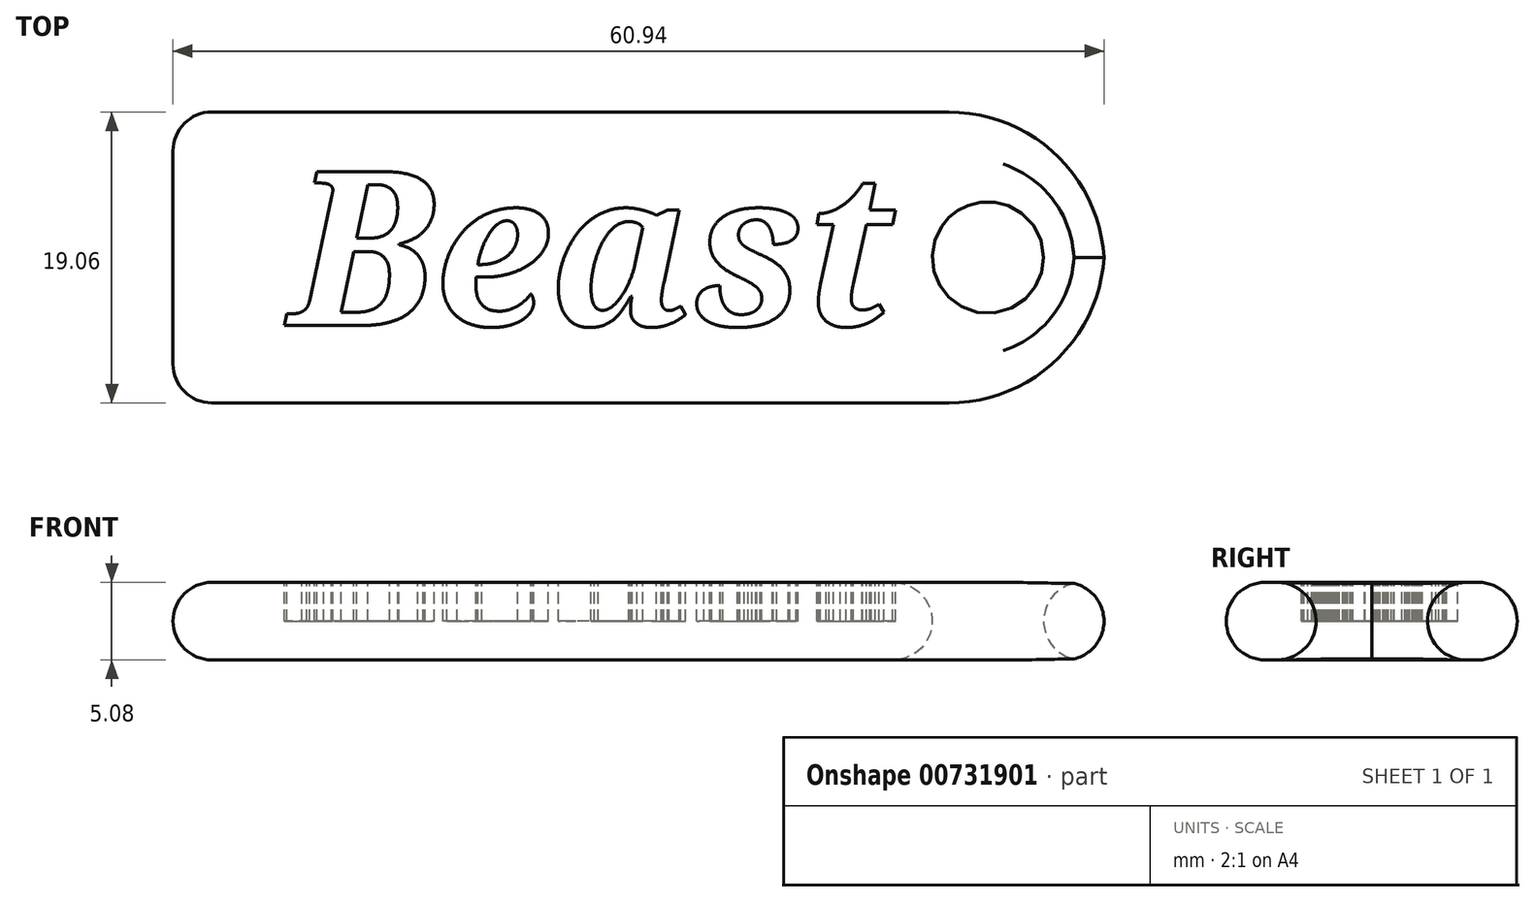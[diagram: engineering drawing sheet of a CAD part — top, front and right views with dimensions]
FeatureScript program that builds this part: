
annotation { "Feature Type Name" : "Feature", "Feature Type Description" : "" }
export const myFeature = defineFeature(function(context is Context, id is Id, definition is map)
    precondition{}
    {
        {
            var Q0;
            Q0=qCreatedBy(makeId("Top.planeOp"),FACE);
            var sketch = newSketch(context, id + "F0", { "sketchPlane" : qUnion([Q0])});
            skLineSegment(sketch, "E0.bottom", {"start": v(20.32, -9.52) * mm, "end": v(-27.94, -9.53) * mm});
            skLineSegment(sketch, "E0.top", {"start": v(20.32, 9.53) * mm, "end": v(-27.94, 9.52) * mm});
            skLineSegment(sketch, "E0.left", {"start": v(30.48, -0.63) * mm, "end": v(30.48, 0.64) * mm});
            skLineSegment(sketch, "E0.right", {"start": v(-30.48, -6.99) * mm, "end": v(-30.48, 6.98) * mm});
            skPoint(sketch, "E0.middle", {"position": v(0, 0) * mm});
            skCircle(sketch, "E1", {"center": v(22.86, 0) * mm, "radius": 3.65 * mm});
            skPoint(sketch, "E2.visualSharp", {"position": v(30.48, 9.53) * mm});
            skArc(sketch, "E2.filletArc", {"start": v(30.48, -0.63) * mm, "mid": v(27.5, 6.55) * mm, "end": v(20.32, 9.53) * mm});
            skPoint(sketch, "E3.visualSharp", {"position": v(30.48, -9.52) * mm});
            skArc(sketch, "E3.filletArc", {"start": v(20.32, -9.53) * mm, "mid": v(27.5, -6.55) * mm, "end": v(30.48, 0.64) * mm});
            skPoint(sketch, "E4.visualSharp", {"position": v(-30.48, 9.52) * mm});
            skArc(sketch, "E4.filletArc", {"start": v(-27.94, 9.52) * mm, "mid": v(-29.74, 8.78) * mm, "end": v(-30.48, 6.98) * mm});
            skPoint(sketch, "E5.visualSharp", {"position": v(-30.48, -9.53) * mm});
            skArc(sketch, "E5.filletArc", {"start": v(-30.48, -6.99) * mm, "mid": v(-29.74, -8.78) * mm, "end": v(-27.94, -9.53) * mm});
            skSolve(sketch);
        }
        {
            var Q0;
            Q0=makeQuery(id+"F0.imprint","IMPRINT",FACE,{"disambiguationData":[TD([[makeQuery(id+"F0.imprint","IMPRINT",EDGE,{"derivedFrom":sQuery(id+"F0.wireOp",EDGE,"E0.bottom")}),-1.0]])]});
            extrude(context, id + "F1", {"entities" : qUnion([Q0]), "depth" : 5.08 * mm, "offsetDistance" : 25.4 * mm});
        }
        {
            var Q0;
            Q0=makeQuery(id+"F1.opExtrude","CAP_FACE",FACE,{"disambiguationData":[OSD([sQuery(id+"F0.wireOp",EDGE,"E0.bottom"),sQuery(id+"F0.wireOp",EDGE,"E0.top"),sQuery(id+"F0.wireOp",EDGE,"E0.left"),sQuery(id+"F0.wireOp",EDGE,"E0.right"),sQuery(id+"F0.wireOp",EDGE,"E1"),sQuery(id+"F0.wireOp",EDGE,"E2.filletArc"),sQuery(id+"F0.wireOp",EDGE,"E3.filletArc"),sQuery(id+"F0.wireOp",EDGE,"E4.filletArc"),sQuery(id+"F0.wireOp",EDGE,"E5.filletArc")])],"isStart":false});
            var sketch = newSketch(context, id + "F2", { "sketchPlane" : qUnion([Q0])});
            skText(sketch, "E6", { "text": "Beast", "fontName": "NotoSerif-BoldItalic.ttf"});
            const initialGuessF2  = {"E6": [-0.02286, -0.00445, 1, 0, 0.01016]};
            skSetInitialGuess(sketch, initialGuessF2);
            skSolve(sketch);
        }
        {
            var Q0;
            Q0 = qSketchRegion(id + "F2", true);
            extrude(context, id + "F3", {"entities" : qUnion([Q0]), "operationType" : NewBodyOperationType.REMOVE, "oppositeDirection" : true, "depth" : 2.54 * mm, "offsetDistance" : 25.4 * mm});
        }
        {
            var Q0;
            Q0=makeQuery(id+"F1.opExtrude","CAP_EDGE",EDGE,{"disambiguationData":[OSD([sQuery(id+"F0.wireOp",EDGE,"E0.bottom")])],"isStart":false});
            var Q1;
            Q1=makeQuery(id+"F1.opExtrude","CAP_EDGE",EDGE,{"disambiguationData":[OSD([sQuery(id+"F0.wireOp",EDGE,"E0.bottom")])],"isStart":true});
            var Q2;
            Q2=makeQuery(id+"F1.opExtrude","CAP_EDGE",EDGE,{"disambiguationData":[OSD([sQuery(id+"F0.wireOp",EDGE,"E1")])],"isStart":false});
            var Q3;
            Q3=makeQuery(id+"F1.opExtrude","CAP_EDGE",EDGE,{"disambiguationData":[OSD([sQuery(id+"F0.wireOp",EDGE,"E1")])],"isStart":true});
            fillet(context, id + "F4", {"entities" : qUnion([Q0, Q1, Q2, Q3]), "radius" : 2.54 * mm, "tangentPropagation" : true, "allowEdgeOverflow" : false});
        }
    });
